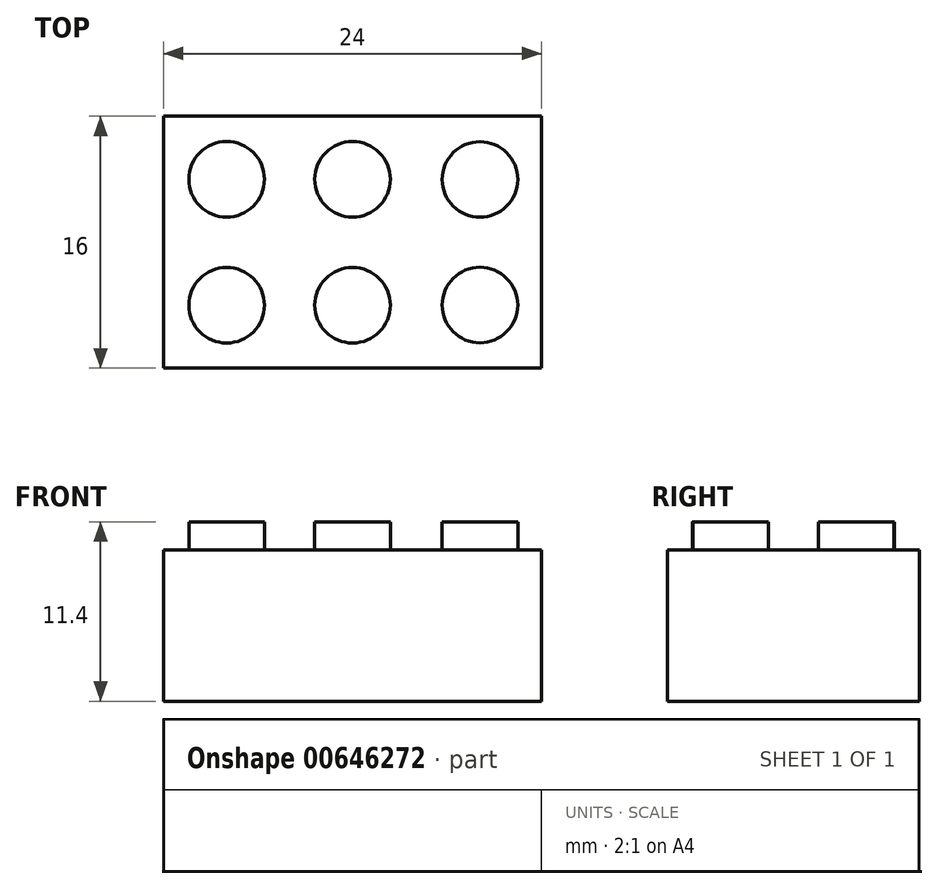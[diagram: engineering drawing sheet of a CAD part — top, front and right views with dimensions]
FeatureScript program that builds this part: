
annotation { "Feature Type Name" : "Feature", "Feature Type Description" : "" }
export const myFeature = defineFeature(function(context is Context, id is Id, definition is map)
    precondition{}
    {
        {
            var Q0;
            Q0=qCreatedBy(makeId("Top.planeOp"),FACE);
            var sketch = newSketch(context, id + "F0", { "sketchPlane" : qUnion([Q0])});
            skLineSegment(sketch, "E0", {"start": v(0, 0) * mm, "end": v(0, 16) * mm});
            skLineSegment(sketch, "E1", {"start": v(0, 16) * mm, "end": v(-24, 16) * mm});
            skLineSegment(sketch, "E2", {"start": v(-24, 16) * mm, "end": v(-24, 0) * mm});
            skLineSegment(sketch, "E3", {"start": v(-24, 0) * mm, "end": v(0, 0) * mm});
            skSolve(sketch);
        }
        {
            var Q0;
            Q0 = qSketchRegion(id + "F0", true);
            var Q1;
            Q1=makeQuery(id+"F0.imprint","IMPRINT",FACE,{"disambiguationData":[TD([[makeQuery(id+"F0.imprint","IMPRINT",EDGE,{"derivedFrom":sQuery(id+"F0.wireOp",EDGE,"E0")}),1.0]])]});
            extrude(context, id + "F1", {"entities" : qUnion([Q0, Q1]), "depth" : 9.6 * mm, "offsetDistance" : 25.4 * mm});
        }
        {
            var Q0;
            Q0=makeQuery(id+"F1.opExtrude","CAP_FACE",FACE,{"disambiguationData":[OSD([sQuery(id+"F0.wireOp",EDGE,"E0"),sQuery(id+"F0.wireOp",EDGE,"E1"),sQuery(id+"F0.wireOp",EDGE,"E2"),sQuery(id+"F0.wireOp",EDGE,"E3")])],"isStart":false});
            var sketch = newSketch(context, id + "F2", { "sketchPlane" : qUnion([Q0])});
            skLineSegment(sketch, "E4", {"start": v(-16, 16) * mm, "end": v(-16, 0) * mm, "construction": true});
            skLineSegment(sketch, "E5", {"start": v(-8, 16) * mm, "end": v(-8, 0) * mm, "construction": true});
            skLineSegment(sketch, "E6", {"start": v(-24, 8) * mm, "end": v(0, 8) * mm, "construction": true});
            skLineSegment(sketch, "E7", {"start": v(-24, 16) * mm, "end": v(-16, 8) * mm, "construction": true});
            skLineSegment(sketch, "E8", {"start": v(-16, 8) * mm, "end": v(-8, 16) * mm, "construction": true});
            skLineSegment(sketch, "E9", {"start": v(-7.82, 15.98) * mm, "end": v(0, 8) * mm, "construction": true});
            skCircle(sketch, "E10", {"center": v(-20, 12) * mm, "radius": 2.4 * mm});
            skCircle(sketch, "E11", {"center": v(-12, 12) * mm, "radius": 2.4 * mm});
            skCircle(sketch, "E12", {"center": v(-3.9, 11.99) * mm, "radius": 2.4 * mm});
            skCircle(sketch, "E13.MirrorC", {"center": v(-3.9, 4.01) * mm, "radius": 2.4 * mm});
            skCircle(sketch, "E14.MirrorC", {"center": v(-12, 4) * mm, "radius": 2.4 * mm});
            skCircle(sketch, "E15.MirrorC", {"center": v(-20, 4) * mm, "radius": 2.4 * mm});
            skSolve(sketch);
        }
        {
            var Q0;
            Q0 = qSketchRegion(id + "F2", true);
            extrude(context, id + "F3", {"entities" : qUnion([Q0]), "operationType" : NewBodyOperationType.ADD, "depth" : 1.8 * mm, "offsetDistance" : 25.4 * mm});
        }
    });
